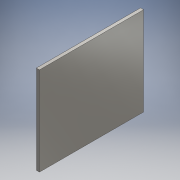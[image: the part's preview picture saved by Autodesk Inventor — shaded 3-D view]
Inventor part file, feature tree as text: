
AUTODESK INVENTOR PART (.ipt)
format: ipt  version: 2016 (Build 200138000, 138)  size: 104,960 bytes
history: native  units: mm
features: extrude x1, sketch x1
ambient origin geometry x8: Origin, YZ Plane, XZ Plane, XY Plane, X Axis, Y Axis, Z Axis, Center Point
bodies: Solid1 (feature_tree)
feature tree (2):
  extrude  "Extrusion1"  Depth=1700.0mm
  sketch  "Sketch1"  dims[d0=2000.0mm d1=1700.0mm d2=60.0mm d3=0.0mm]
